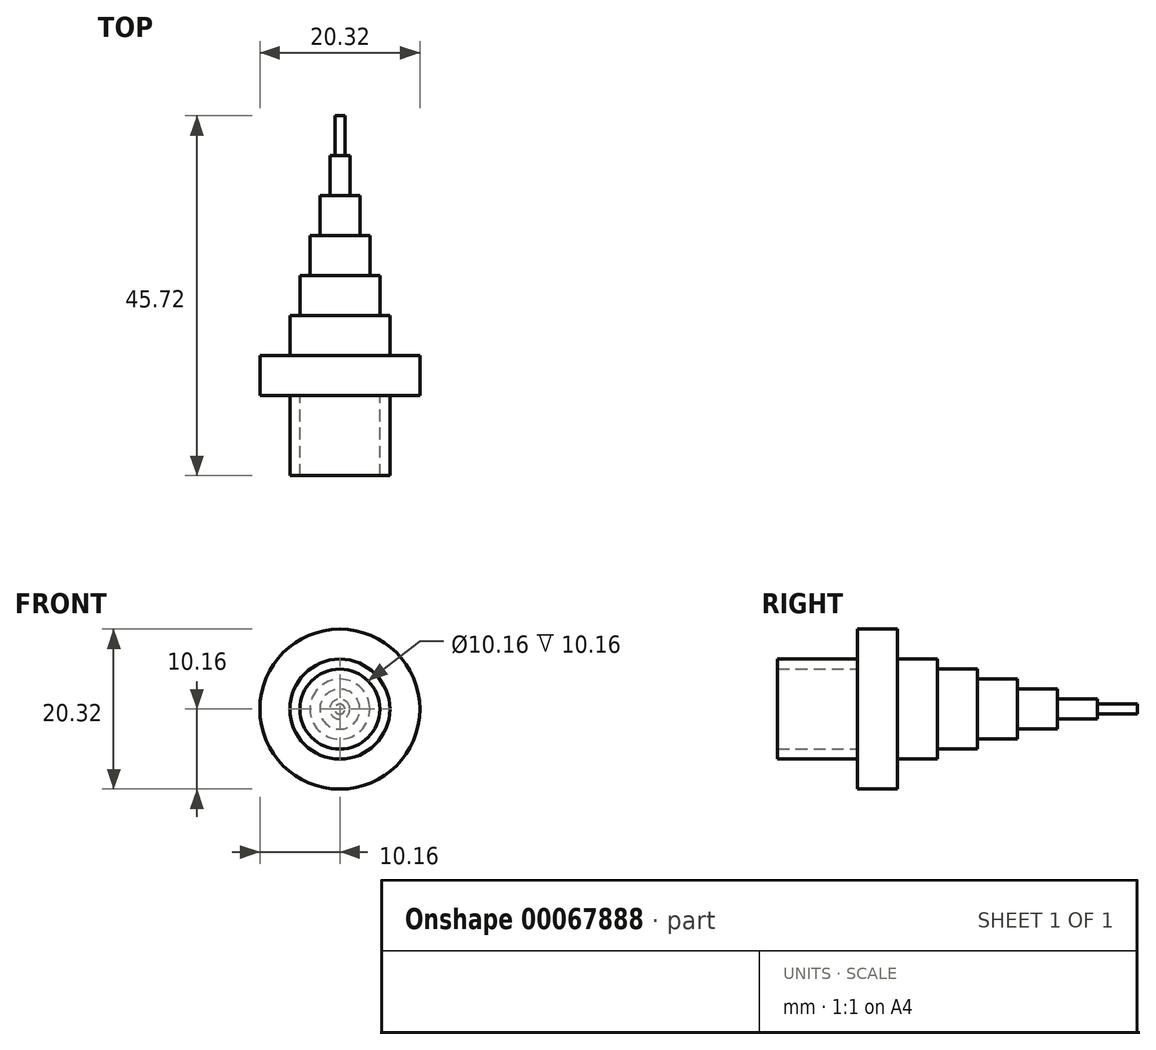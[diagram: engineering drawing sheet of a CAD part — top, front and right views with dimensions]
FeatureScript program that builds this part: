
annotation { "Feature Type Name" : "Feature", "Feature Type Description" : "" }
export const myFeature = defineFeature(function(context is Context, id is Id, definition is map)
    precondition{}
    {
        {
            var Q0;
            Q0=qCreatedBy(makeId("Front.planeOp"),FACE);
            var sketch = newSketch(context, id + "F0", { "sketchPlane" : qUnion([Q0])});
            skCircle(sketch, "E0", {"center": v(0, 0) * mm, "radius": 10.16 * mm});
            skSolve(sketch);
        }
        {
            var Q0;
            Q0=makeQuery(id+"F0.imprint","IMPRINT",FACE,{"disambiguationData":[TD([[makeQuery(id+"F0.imprint","IMPRINT",EDGE,{"derivedFrom":sQuery(id+"F0.wireOp",EDGE,"E0")}),1.0]])]});
            extrude(context, id + "F1", {"entities" : qUnion([Q0]), "depth" : 5.08 * mm});
        }
        {
            var Q0;
            Q0=makeQuery(id+"F1.opExtrude","CAP_FACE",FACE,{"disambiguationData":[OSD([sQuery(id+"F0.wireOp",EDGE,"E0")])],"isStart":false});
            var sketch = newSketch(context, id + "F2", { "sketchPlane" : qUnion([Q0])});
            skCircle(sketch, "E1", {"center": v(0, 0) * mm, "radius": 6.35 * mm});
            skCircle(sketch, "E2", {"center": v(0, 0) * mm, "radius": 5.08 * mm});
            skSolve(sketch);
        }
        {
            var Q0;
            Q0=makeQuery(id+"F2.imprint","IMPRINT",FACE,{"disambiguationData":[TD([[makeQuery(id+"F2.imprint","IMPRINT",EDGE,{"derivedFrom":sQuery(id+"F2.wireOp",EDGE,"E1")}),1.0]])]});
            extrude(context, id + "F3", {"entities" : qUnion([Q0]), "operationType" : NewBodyOperationType.ADD, "depth" : 10.16 * mm});
        }
        {
            var Q0;
            Q0=makeQuery(id+"F1.opExtrude","CAP_FACE",FACE,{"disambiguationData":[OSD([sQuery(id+"F0.wireOp",EDGE,"E0")])],"isStart":true});
            var sketch = newSketch(context, id + "F4", { "sketchPlane" : qUnion([Q0])});
            skCircle(sketch, "E3", {"center": v(0, 0) * mm, "radius": 6.35 * mm});
            skSolve(sketch);
        }
        {
            var Q0;
            Q0=makeQuery(id+"F4.imprint","IMPRINT",FACE,{"disambiguationData":[TD([[makeQuery(id+"F4.imprint","IMPRINT",EDGE,{"derivedFrom":sQuery(id+"F4.wireOp",EDGE,"E3")}),1.0]])]});
            extrude(context, id + "F5", {"entities" : qUnion([Q0]), "operationType" : NewBodyOperationType.ADD, "depth" : 5.08 * mm});
        }
        {
            var Q0;
            Q0=makeQuery(id+"F5.opExtrude","CAP_FACE",FACE,{"disambiguationData":[OSD([sQuery(id+"F4.wireOp",EDGE,"E3")])],"isStart":false});
            var sketch = newSketch(context, id + "F6", { "sketchPlane" : qUnion([Q0])});
            skCircle(sketch, "E4", {"center": v(0, 0) * mm, "radius": 5.08 * mm});
            skSolve(sketch);
        }
        {
            var Q0;
            Q0=makeQuery(id+"F6.imprint","IMPRINT",FACE,{"disambiguationData":[TD([[makeQuery(id+"F6.imprint","IMPRINT",EDGE,{"derivedFrom":sQuery(id+"F6.wireOp",EDGE,"E4")}),1.0]])]});
            extrude(context, id + "F7", {"entities" : qUnion([Q0]), "operationType" : NewBodyOperationType.ADD, "depth" : 5.08 * mm});
        }
        {
            var Q0;
            Q0=makeQuery(id+"F7.opExtrude","CAP_FACE",FACE,{"disambiguationData":[OSD([sQuery(id+"F6.wireOp",EDGE,"E4")])],"isStart":false});
            var sketch = newSketch(context, id + "F8", { "sketchPlane" : qUnion([Q0])});
            skCircle(sketch, "E5", {"center": v(0, 0) * mm, "radius": 3.81 * mm});
            skSolve(sketch);
        }
        {
            var Q0;
            Q0=makeQuery(id+"F8.imprint","IMPRINT",FACE,{"disambiguationData":[TD([[makeQuery(id+"F8.imprint","IMPRINT",EDGE,{"derivedFrom":sQuery(id+"F8.wireOp",EDGE,"E5")}),1.0]])]});
            extrude(context, id + "F9", {"entities" : qUnion([Q0]), "operationType" : NewBodyOperationType.ADD, "depth" : 5.08 * mm});
        }
        {
            var Q0;
            Q0=makeQuery(id+"F9.opExtrude","CAP_FACE",FACE,{"disambiguationData":[OSD([sQuery(id+"F8.wireOp",EDGE,"E5")])],"isStart":false});
            var sketch = newSketch(context, id + "F10", { "sketchPlane" : qUnion([Q0])});
            skCircle(sketch, "E6", {"center": v(0, 0) * mm, "radius": 2.54 * mm});
            skSolve(sketch);
        }
        {
            var Q0;
            Q0=makeQuery(id+"F10.imprint","IMPRINT",FACE,{"disambiguationData":[TD([[makeQuery(id+"F10.imprint","IMPRINT",EDGE,{"derivedFrom":sQuery(id+"F10.wireOp",EDGE,"E6")}),1.0]])]});
            extrude(context, id + "F11", {"entities" : qUnion([Q0]), "operationType" : NewBodyOperationType.ADD, "depth" : 5.08 * mm});
        }
        {
            var Q0;
            Q0=makeQuery(id+"F11.opExtrude","CAP_FACE",FACE,{"disambiguationData":[OSD([sQuery(id+"F10.wireOp",EDGE,"E6")])],"isStart":false});
            var sketch = newSketch(context, id + "F12", { "sketchPlane" : qUnion([Q0])});
            skCircle(sketch, "E7", {"center": v(0, 0) * mm, "radius": 1.27 * mm});
            skSolve(sketch);
        }
        {
            var Q0;
            Q0=makeQuery(id+"F12.imprint","IMPRINT",FACE,{"disambiguationData":[TD([[makeQuery(id+"F12.imprint","IMPRINT",EDGE,{"derivedFrom":sQuery(id+"F12.wireOp",EDGE,"E7")}),1.0]])]});
            extrude(context, id + "F13", {"entities" : qUnion([Q0]), "operationType" : NewBodyOperationType.ADD, "depth" : 5.08 * mm});
        }
        {
            var Q0;
            Q0=makeQuery(id+"F13.opExtrude","CAP_FACE",FACE,{"disambiguationData":[OSD([sQuery(id+"F12.wireOp",EDGE,"E7")])],"isStart":false});
            var sketch = newSketch(context, id + "F14", { "sketchPlane" : qUnion([Q0])});
            skCircle(sketch, "E8", {"center": v(0, 0) * mm, "radius": 0.64 * mm});
            skSolve(sketch);
        }
        {
            var Q0;
            Q0=makeQuery(id+"F14.imprint","IMPRINT",FACE,{"disambiguationData":[TD([[makeQuery(id+"F14.imprint","IMPRINT",EDGE,{"derivedFrom":sQuery(id+"F14.wireOp",EDGE,"E8")}),1.0]])]});
            extrude(context, id + "F15", {"entities" : qUnion([Q0]), "operationType" : NewBodyOperationType.ADD, "depth" : 5.08 * mm});
        }
    });
